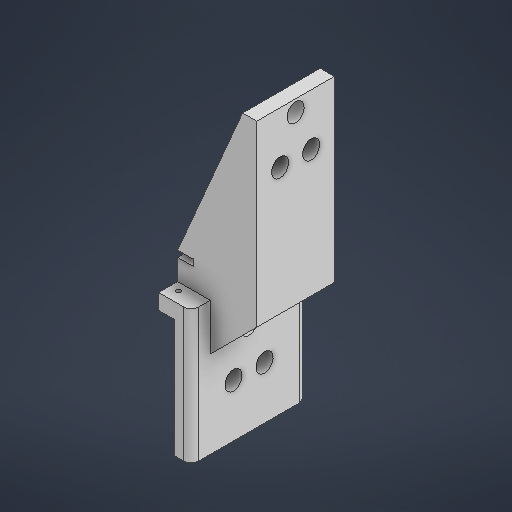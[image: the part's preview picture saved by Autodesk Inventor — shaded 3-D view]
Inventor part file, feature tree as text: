
AUTODESK INVENTOR PART (.ipt)
format: ipt  version: 2025 (Build 290162000, 162)  size: 346,624 bytes
history: native  units: in
note: dims shown in document units (in); Inventor stores cm internally (conversion verified against a paired STEP export)
features: extrude x13, sketch x10, plane x5, chamfer x2, fillet x1
ambient origin geometry x8: Origin, YZ Plane, XZ Plane, XY Plane, X Axis, Y Axis, Z Axis, Center Point
bodies: Solid1 (feature_tree)
feature tree (31):
  sketch  "Sketch1"  dims[d0=0.4331in d1=2.9331in]
  extrude  "Extrusion1"  Depth=2.9331in
  extrude  "Extrusion2"  Depth=0.2854in
  extrude  "Extrusion3"  Depth=0.3937in TaperAngle=0.0deg
  plane  "Work Plane1"
  plane  "Work Plane3"
  sketch  "Sketch4"  dims[d9=0.4213in d10=2.9921in d11=0.0in]
  extrude  "Extrusion4"  Depth=2.9921in TaperAngle=0.0deg
  extrude  "Extrusion11"  Depth=0.1575in
  extrude  "Extrusion6"  Depth=0.1575in
  extrude  "Extrusion7"  Depth=0.3937in
  extrude  "Extrusion8"  Depth=2.1457in
  chamfer  "Chamfer1"  [1 undecoded]
  sketch  "Sketch6"  dims[d14=0.4331in d15=0.1575in d16=0.4331in]
  extrude  "Extrusion9"  Depth=4.9213in TaperAngle=0.0deg
  chamfer  "Chamfer2"  Distance=1.5748in
  extrude  "Extrusion12"  Depth=1.9685in
  plane  "Work Plane4"
  extrude  "Extrusion13"  TaperAngle=0.0deg  [1 undecoded]
  plane  "Work Plane5"
  plane  "Work Plane6"
  extrude  "Extrusion14"  Depth=1.1811in
  extrude  "Extrusion15"  Depth=0.1969in
  fillet  "Fillet1"  Radius=1.0207in
  sketch  "Sketch2"  dims[d2=0.1181in d3=0.2854in]
  sketch  "Sketch3"  dims[d5=0.3937in d6=0.0in d7=0.3937in d8=0.0in]
  sketch  "Sketch5"  dims[d12=1.0668in d13=0.1575in]
  sketch  "Sketch8"  dims[d19=0.3937in d20=0.9331in]
  sketch  "Sketch9"  dims[d21=0.5906in d22=0.0in d23=2.1457in d26=0.0in d27=0.0in]
  sketch  "Sketch10"  dims[d28=1.9685in d29=4.9213in d30=0.0in d31=1.5748in d32=0.0in]
  sketch  "Sketch11"  dims[d33=1.5748in d34=0.0787in d35=0.1598in d36=0.1575in d37=0.4331in d38=0.1575in d39=0.4331in d40=0.3937in d41=0.9331in d44=1.9685in d46=0.0in d47=0.0in d51=1.1811in d52=1.1811in d53=0.7782in d56=0.1969in d57=1.0207in d58=0.0in d59=1.9685in d60=0.8937in d61=0.0in d62=-1.378in d63=0.4331in d64=0.4331in d65=0.4331in d66=1.1393in d67=0.0in d68=0.0in d69=90.0deg d70=1.9685in d71=0.5906in d72=2.7756in d73=2.1393in d74=0.0in d75=0.0in d76=0.3937in d77=0.1575in d78=2.7756in d79=0.0in d80=0.1969in]
note: 2 required parameter values undecoded (feature->parameter linkage not recoverable at this tier; creation-order binding heuristic only, values carry confidence <= 0.55)
